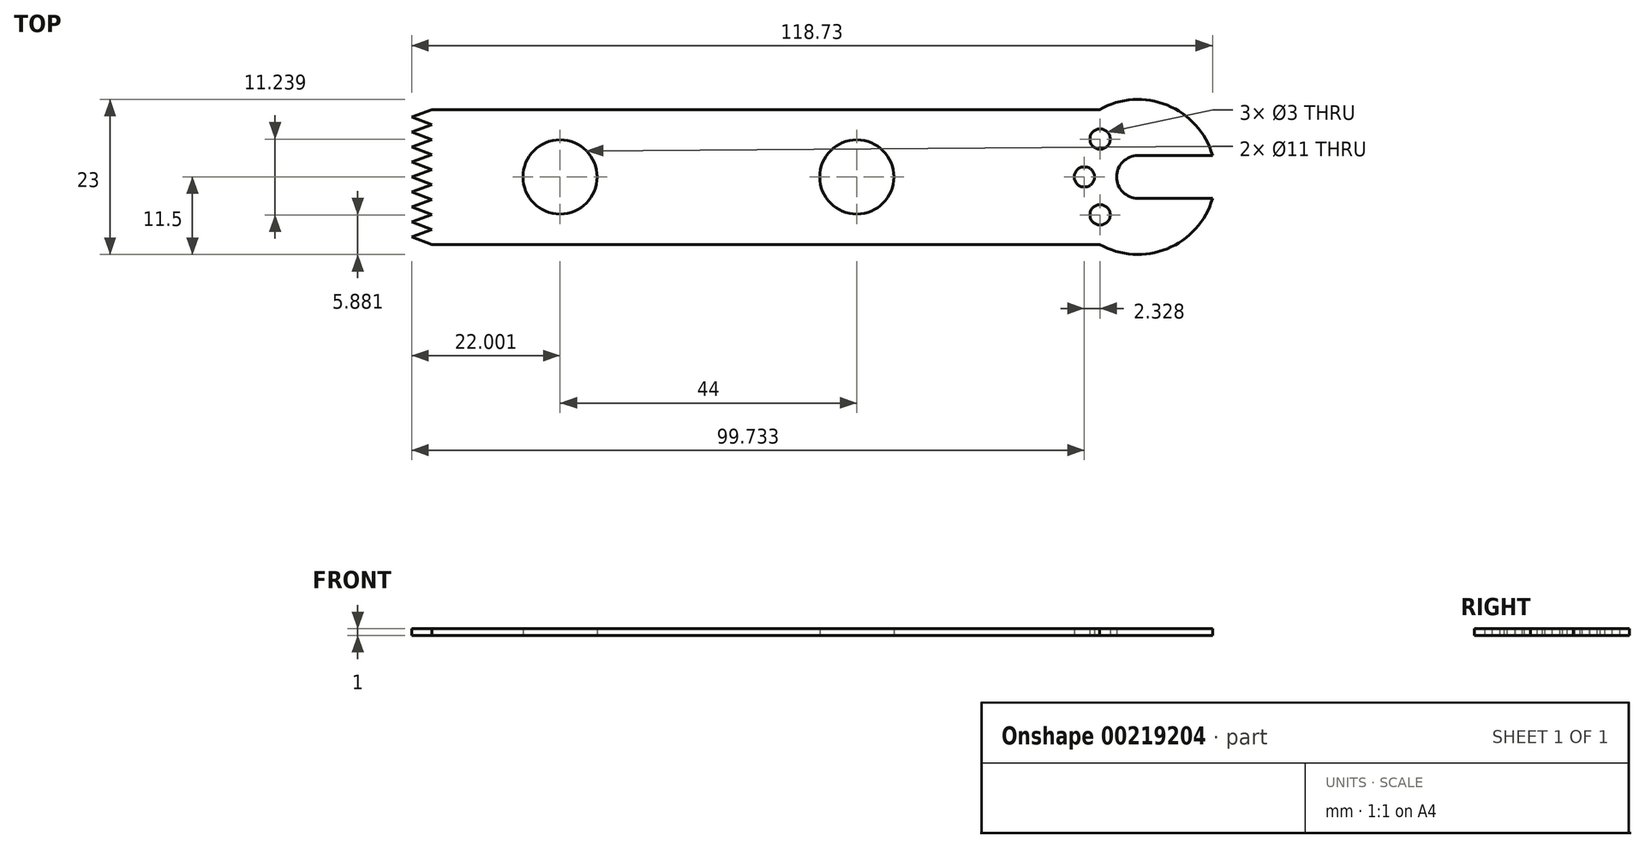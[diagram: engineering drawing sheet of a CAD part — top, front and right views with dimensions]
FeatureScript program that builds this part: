
annotation { "Feature Type Name" : "Feature", "Feature Type Description" : "" }
export const myFeature = defineFeature(function(context is Context, id is Id, definition is map)
    precondition{}
    {
        {
            var Q0;
            Q0=qCreatedBy(makeId("Top.planeOp"),FACE);
            var sketch = newSketch(context, id + "F0", { "sketchPlane" : qUnion([Q0])});
            skArc(sketch, "E0", {"start": v(-5.68, -10) * mm, "mid": v(4.34, -10.65) * mm, "end": v(11.05, -3.18) * mm});
            skLineSegment(sketch, "E1", {"start": v(0, 0) * mm, "end": v(-115.37, 0) * mm, "construction": true});
            skLineSegment(sketch, "E2", {"start": v(-5.68, 10) * mm, "end": v(-107.68, 10) * mm});
            skLineSegment(sketch, "E3", {"start": v(-5.68, -10) * mm, "end": v(-107.68, -10) * mm});
            skLineSegment(sketch, "E4", {"start": v(-107.68, -10) * mm, "end": v(-107.68, 10) * mm});
            skArc(sketch, "E5", {"start": v(0, 3.17) * mm, "mid": v(-3.17, 0) * mm, "end": v(0, -3.17) * mm});
            skLineSegment(sketch, "E6", {"start": v(0, 3.17) * mm, "end": v(11.05, 3.17) * mm});
            skLineSegment(sketch, "E7", {"start": v(0, -3.17) * mm, "end": v(11.05, -3.17) * mm});
            skArc(sketch, "E8.trimOffspring", {"start": v(11.05, 3.18) * mm, "mid": v(4.34, 10.65) * mm, "end": v(-5.68, 10) * mm});
            skCircle(sketch, "E9", {"center": v(-85.68, 0) * mm, "radius": 5.5 * mm});
            skCircle(sketch, "E10", {"center": v(-41.68, 0) * mm, "radius": 5.5 * mm});
            skCircle(sketch, "E11", {"center": v(-7.95, 0) * mm, "radius": 1.5 * mm});
            skCircle(sketch, "E12.1.0", {"center": v(-5.62, 5.62) * mm, "radius": 1.5 * mm});
            skLineSegment(sketch, "E12.anchor1", {"start": v(0, 0) * mm, "end": v(-7.95, 0) * mm, "construction": true});
            skLineSegment(sketch, "E12.anchor2", {"start": v(0, 0) * mm, "end": v(-5.62, 5.62) * mm, "construction": true});
            skCircle(sketch, "E13.MirrorC", {"center": v(-5.62, -5.62) * mm, "radius": 1.5 * mm});
            skLineSegment(sketch, "E14.0", {"start": v(-104.68, -10) * mm, "end": v(-104.68, 10) * mm, "construction": true});
            skLineSegment(sketch, "E15", {"start": v(-104.68, -10) * mm, "end": v(-107.68, -8.89) * mm});
            skLineSegment(sketch, "E16", {"start": v(-107.68, -8.9) * mm, "end": v(-104.68, -7.78) * mm});
            skLineSegment(sketch, "E17", {"start": v(-104.68, -7.78) * mm, "end": v(-107.68, -6.67) * mm});
            skLineSegment(sketch, "E18", {"start": v(-107.68, -6.67) * mm, "end": v(-104.68, -5.56) * mm});
            skLineSegment(sketch, "E19", {"start": v(-104.68, -5.56) * mm, "end": v(-107.68, -4.45) * mm});
            skLineSegment(sketch, "E20", {"start": v(-107.68, -4.45) * mm, "end": v(-104.68, -3.34) * mm});
            skLineSegment(sketch, "E21", {"start": v(-104.68, -3.34) * mm, "end": v(-107.68, -2.23) * mm});
            skLineSegment(sketch, "E22", {"start": v(-107.68, -2.23) * mm, "end": v(-104.68, -1.12) * mm});
            skLineSegment(sketch, "E23", {"start": v(-104.68, -1.12) * mm, "end": v(-107.68, -0.01) * mm});
            skLineSegment(sketch, "E24", {"start": v(-107.68, -0.01) * mm, "end": v(-104.68, 1.1) * mm});
            skLineSegment(sketch, "E25", {"start": v(-104.68, 1.1) * mm, "end": v(-107.68, 2.2) * mm});
            skLineSegment(sketch, "E26", {"start": v(-107.68, 2.2) * mm, "end": v(-104.68, 3.32) * mm});
            skLineSegment(sketch, "E27", {"start": v(-104.68, 3.32) * mm, "end": v(-107.68, 4.43) * mm});
            skLineSegment(sketch, "E28", {"start": v(-107.68, 4.43) * mm, "end": v(-104.68, 5.54) * mm});
            skLineSegment(sketch, "E29", {"start": v(-104.68, 5.54) * mm, "end": v(-107.68, 6.65) * mm});
            skLineSegment(sketch, "E30", {"start": v(-107.68, 6.65) * mm, "end": v(-104.68, 7.76) * mm});
            skLineSegment(sketch, "E31", {"start": v(-104.68, 7.76) * mm, "end": v(-107.68, 8.87) * mm});
            skLineSegment(sketch, "E32", {"start": v(-107.68, 8.87) * mm, "end": v(-104.68, 10) * mm});
            skSolve(sketch);
        }
        {
            var Q0;
            Q0=makeQuery(id+"F0.imprint","IMPRINT",FACE,{"disambiguationData":[TD([[makeQuery(id+"F0.imprint","IMPRINT",EDGE,{"derivedFrom":sQuery(id+"F0.wireOp",EDGE,"E0")}),1.0]])]});
            extrude(context, id + "F1", {"entities" : qUnion([Q0]), "depth" : 1 * mm});
        }
    });
